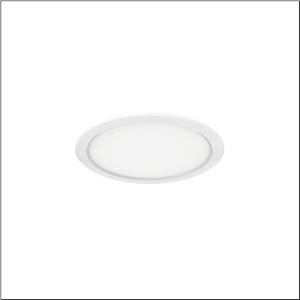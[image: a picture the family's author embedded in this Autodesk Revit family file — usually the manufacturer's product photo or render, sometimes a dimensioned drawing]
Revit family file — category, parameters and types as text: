
# Revit family: lunis_41_eco_51ds107f44a
name_source: partatom
category: Lighting Fixtures
units: mm (PartAtom-declared; Revit-internal decimal feet)

## family parameters
Cut with Voids When Loaded = No
Host = Face
Light Source = No
Part Type = Normal
Room Calculation Point = No
Round Connector Dimension = Use Diameter
Shared = No

## types (1)
- Lunis 41 ECO (1 x LED, 2300 lm, 22 W, 4000K)
    Apparent Load = 22 VA
    CIE Flux Codes = 47 80 97 100 100
    Color Rendering = 80
    Color Temperature = 4000K
    Default Elevation = 1800 mm
    Description = Lunis 41,  ECO, downlight, light emission: direct distribution, LED rated luminous flux: 2.300lm, light colour: 840, control gear: ECG, mains connection: 230V, AC, 50/60Hz, housing, round, of aluminium, coated, traffic white (RAL 9016), diameter: 216mm, recess depth: 58mm, protection rating (complete): IP20, protection rating (on room side): IP40, insulation class (complete): insulation class II (safety insulation), certification: CE, permissible ambient temperature for indoor applications: -20..+40°C, packaging unit: 1 piece
    Height = 0 mm  [stored 0 ft]
    Lamp = 1 x LED
    Lamp Light Flux = 2300 lm
    Lamp Power = 22 W
    Lamp count = 1
    Length = 216 mm
    Luminous efficacy = 105 lm/W
    Manufacturer = Siteco
    ModVariant = No
    Model = 51DS107F44A
    Mounting Place = Ceiling
    Mounting Type = Recessed
    Number of Poles = 1
    OnlyDefault = Yes
    Power Factor = 1
    Product Name = Lunis 41 ECO
    Product group = downlight
    ProductGroupID = 401
    Protection Class = Protection class II
    Protection Degree = IP 20
    RLX_Detail_Level = 1
    RLX_Emergency_Light_Flux = 0 lm
    RLX_Emergency_Type = 0
    RLX_Emergency_Type_DB = No
    RlxData = <blob elided: 22569 chars, md5=573e1511>
    Socket = socket
    Standby Power = 0 W
    System Light Flux = 2300 lm
    System Power = 22 W
    Type Comments = Product without accessories
    Type Image = l_1007043.jpg
    URL = http://relux.com
    VarID = ---
    Voltage = 0 V
    Weight = 0.00 kg
    Width = 0 mm  [stored 0 ft]

note: [stored X ft] marks values corroborated as IEEE doubles in the binary element streams (Revit-internal decimal feet)

## geometry (parser evidence)
native form markers: Blend x4, Sweep x12
no freeform markers — native parametric forms only
